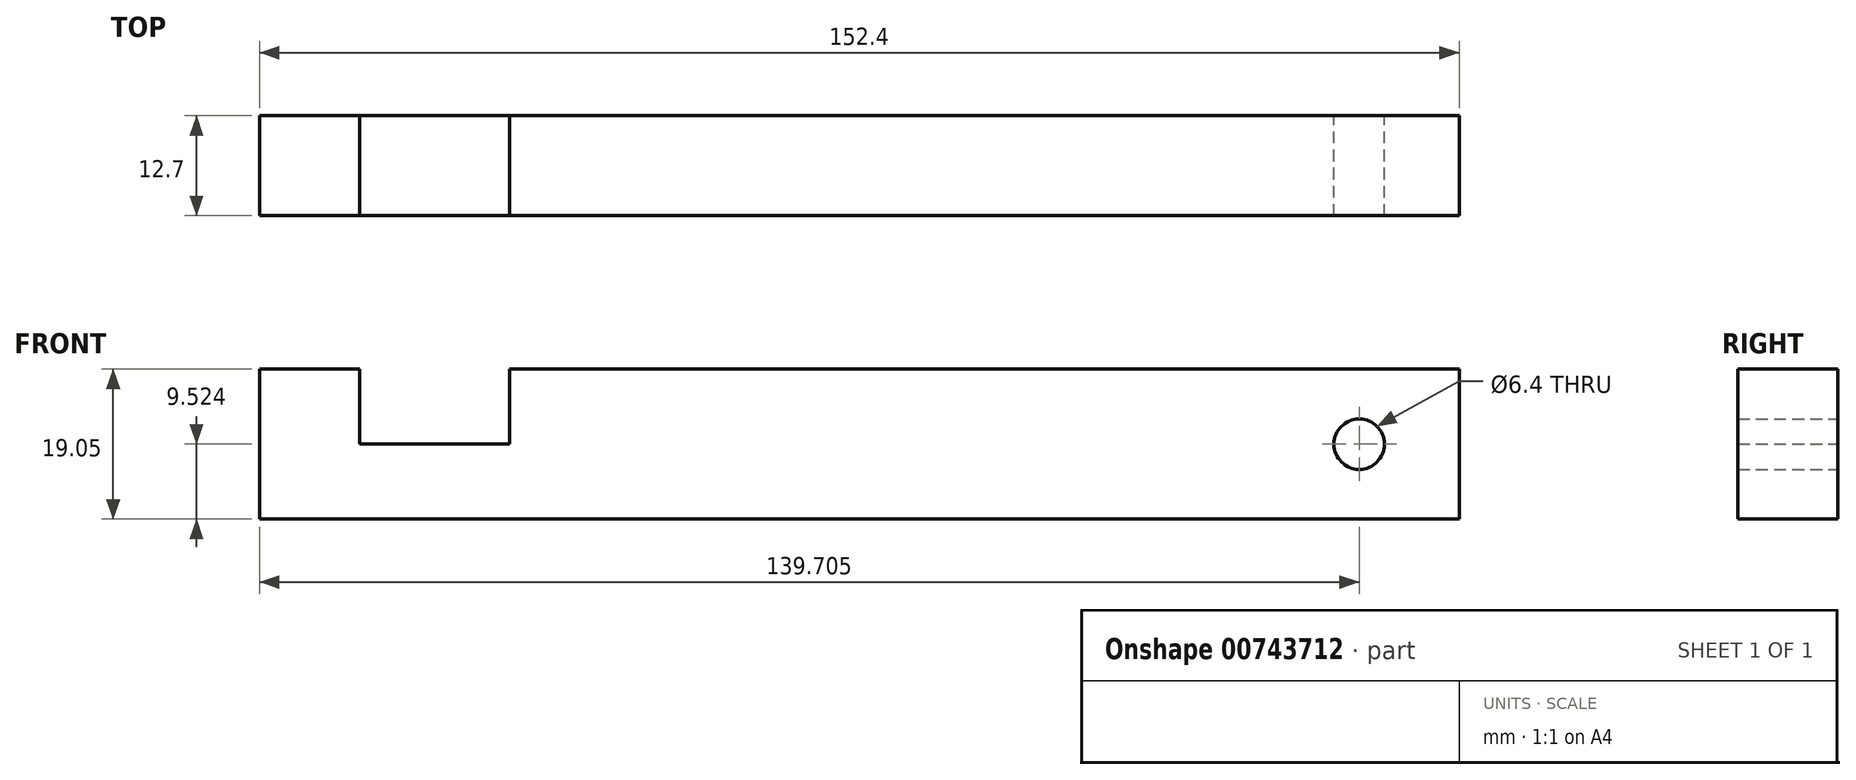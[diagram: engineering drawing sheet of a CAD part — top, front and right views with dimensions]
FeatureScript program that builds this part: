
annotation { "Feature Type Name" : "Feature", "Feature Type Description" : "" }
export const myFeature = defineFeature(function(context is Context, id is Id, definition is map)
    precondition{}
    {
        {
            var Q0;
            Q0=qCreatedBy(makeId("Front.planeOp"),FACE);
            var sketch = newSketch(context, id + "F0", { "sketchPlane" : qUnion([Q0])});
            skLineSegment(sketch, "E0.bottom", {"start": v(-69, -3.76) * mm, "end": v(83.4, -3.76) * mm});
            skLineSegment(sketch, "E0.top", {"start": v(-69, -22.81) * mm, "end": v(83.4, -22.81) * mm});
            skLineSegment(sketch, "E0.left", {"start": v(-69, -3.76) * mm, "end": v(-69, -22.81) * mm});
            skLineSegment(sketch, "E0.right", {"start": v(83.4, -3.76) * mm, "end": v(83.4, -22.81) * mm});
            skLineSegment(sketch, "E1.bottom", {"start": v(-56.3, -3.76) * mm, "end": v(-37.26, -3.76) * mm});
            skLineSegment(sketch, "E1.top", {"start": v(-56.3, -13.29) * mm, "end": v(-37.26, -13.29) * mm});
            skLineSegment(sketch, "E1.left", {"start": v(-56.3, -3.76) * mm, "end": v(-56.3, -13.29) * mm});
            skLineSegment(sketch, "E1.right", {"start": v(-37.26, -3.76) * mm, "end": v(-37.26, -13.29) * mm});
            skCircle(sketch, "E2", {"center": v(70.7, -13.29) * mm, "radius": 3.2 * mm});
            skSolve(sketch);
        }
        {
            var Q0;
            Q0=makeQuery(id+"F0.imprint","IMPRINT",FACE,{"disambiguationData":[TD([[makeQuery(id+"F0.imprint","IMPRINT",EDGE,{"derivedFrom":sQuery(id+"F0.wireOp",EDGE,"E0.top")}),1.0]])]});
            extrude(context, id + "F1", {"entities" : qUnion([Q0]), "depth" : 12.7 * mm, "offsetDistance" : 25.4 * mm});
        }
    });
